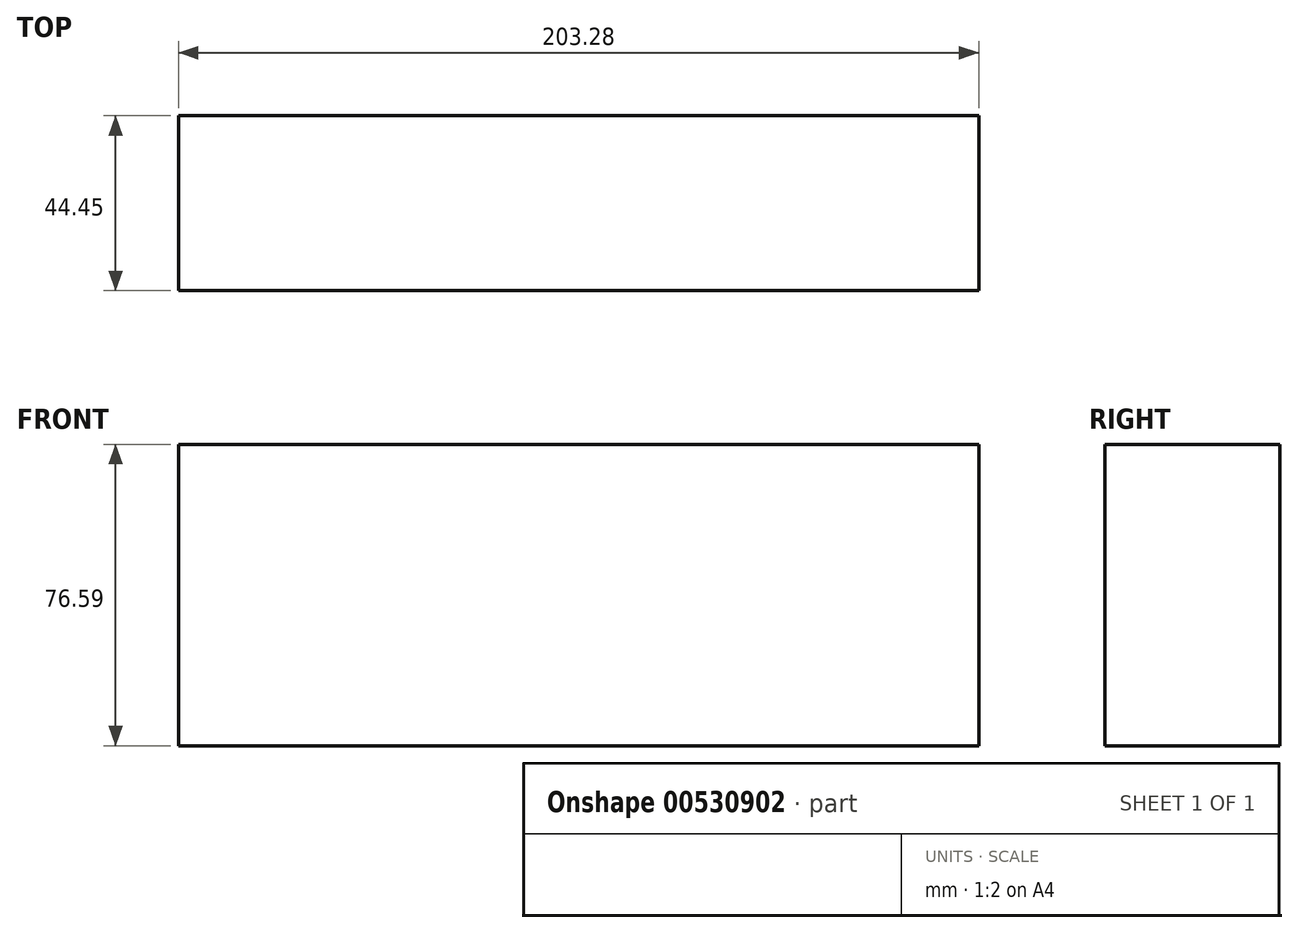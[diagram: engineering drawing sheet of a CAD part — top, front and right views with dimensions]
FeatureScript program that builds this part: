
annotation { "Feature Type Name" : "Feature", "Feature Type Description" : "" }
export const myFeature = defineFeature(function(context is Context, id is Id, definition is map)
    precondition{}
    {
        {
            var Q0;
            Q0=qCreatedBy(makeId("Front.planeOp"),FACE);
            var sketch = newSketch(context, id + "F0", { "sketchPlane" : qUnion([Q0])});
            skLineSegment(sketch, "E0", {"start": v(-95.35, -22.62) * mm, "end": v(107.93, -22.62) * mm});
            skLineSegment(sketch, "E1", {"start": v(107.93, -22.62) * mm, "end": v(107.93, 53.97) * mm});
            skLineSegment(sketch, "E2", {"start": v(107.93, 53.97) * mm, "end": v(-95.35, 53.97) * mm});
            skLineSegment(sketch, "E3", {"start": v(-95.35, 53.97) * mm, "end": v(-95.35, -22.62) * mm});
            skLineSegment(sketch, "E4", {"start": v(107.93, 31.23) * mm, "end": v(-95.35, 31.23) * mm});
            skSolve(sketch);
        }
        {
            var Q0;
            Q0 = qSketchRegion(id + "F0", true);
            extrude(context, id + "F1", {"entities" : qUnion([Q0]), "depth" : 44.45 * mm, "offsetDistance" : 25.4 * mm});
        }
    });
